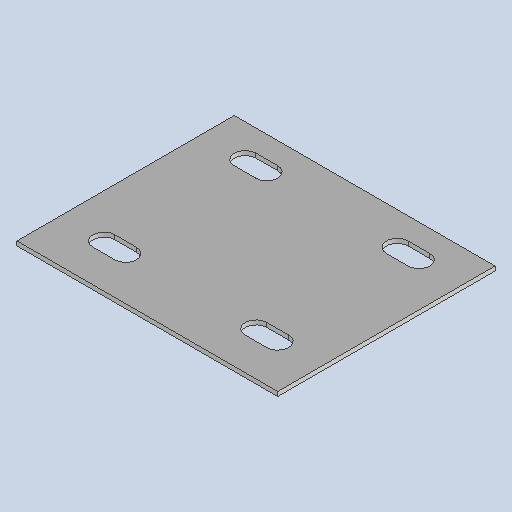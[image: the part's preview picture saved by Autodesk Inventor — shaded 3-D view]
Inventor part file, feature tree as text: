
AUTODESK INVENTOR PART (.ipt)
format: ipt  version: 2025 (Build 290162010, 162A)  size: 276,480 bytes
history: native  units: mm
features: other x5, sketch x3, sheet_metal_op x1, pattern_linear x1, projected_geometry x1
ambient origin geometry x8: Origin, YZ Plane, XZ Plane, XY Plane, X Axis, Y Axis, Z Axis, Center Point
bodies: Solid1 (feature_tree)
feature tree (11):
  sheet_metal_op  "Face1"
  other  "Mark1"
  other  "A-Side Definition"
  pattern_linear  "Rectangular Pattern1"  Count1=12  [1 undecoded]
  sketch  "Sketch1"  dims[d1=100.0mm]
  other  "Plate1"
  sketch  "Sketch2"  dims[d2=2.0mm]
  sketch  "Sketch3"  dims[d6=200.0mm d9=20.0mm d10=20.0mm d11=20.0mm d17=5.0mm d18=10.0mm d19=5.0mm d20=10.0mm d21=15.0mm d22=25.0mm d23=2.0mm d24=0.0mm d25=20.0mm d27=65.0mm d28=20.0mm d30=70.0mm]
  projected_geometry  "Projected Loop1"
  other  "Cut1"
  other  "Definition1"
note: 1 required parameter value undecoded (feature->parameter linkage not recoverable at this tier; creation-order binding heuristic only, values carry confidence <= 0.55)
